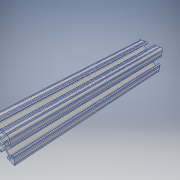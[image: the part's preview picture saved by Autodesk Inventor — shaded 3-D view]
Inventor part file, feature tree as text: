
AUTODESK INVENTOR PART (.ipt)
format: ipt  version: 2019 (Build 230136000, 136)  size: 333,824 bytes
history: native  units: in
note: dims shown in document units (in); Inventor stores cm internally (conversion verified against a paired STEP export)
features: other x1, extrude x1, sketch x1, projected_geometry x1
ambient origin geometry x8: Origin, YZ Plane, XZ Plane, XY Plane, X Axis, Y Axis, Z Axis, Center Point
bodies: Solid1 (feature_tree)
feature tree (4):
  other  "Boss-Extrude1"
  extrude  "Extrusion2"  [1 undecoded]
  sketch  "Sketch2"  dims[d2=6.0in d3=0.0in]
  projected_geometry  "Projected Loop2"
note: 1 required parameter value undecoded (feature->parameter linkage not recoverable at this tier; creation-order binding heuristic only, values carry confidence <= 0.55)
